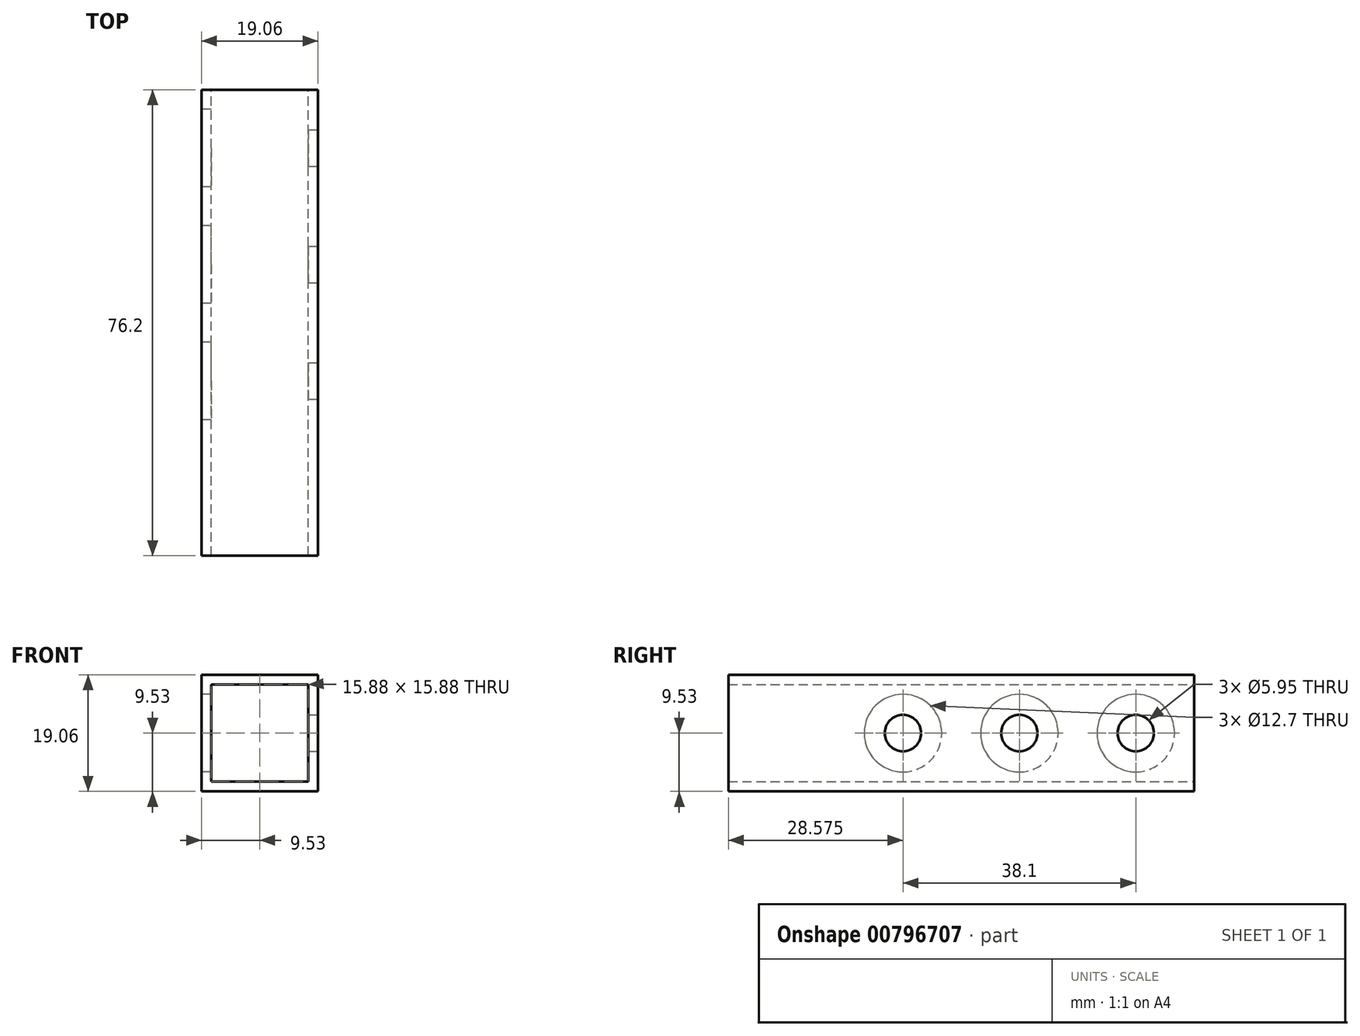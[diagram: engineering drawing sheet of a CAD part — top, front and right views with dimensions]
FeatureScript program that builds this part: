
annotation { "Feature Type Name" : "Feature", "Feature Type Description" : "" }
export const myFeature = defineFeature(function(context is Context, id is Id, definition is map)
    precondition{}
    {
        {
            var Q0;
            Q0=qCreatedBy(makeId("Front.planeOp"),FACE);
            var sketch = newSketch(context, id + "F0", { "sketchPlane" : qUnion([Q0])});
            skLineSegment(sketch, "E0.bottom", {"start": v(-9.52, 9.53) * mm, "end": v(9.53, 9.53) * mm});
            skLineSegment(sketch, "E0.top", {"start": v(-9.53, -9.53) * mm, "end": v(9.52, -9.53) * mm});
            skLineSegment(sketch, "E0.left", {"start": v(-9.52, 9.53) * mm, "end": v(-9.53, -9.52) * mm});
            skLineSegment(sketch, "E0.right", {"start": v(9.53, 9.53) * mm, "end": v(9.52, -9.52) * mm});
            skPoint(sketch, "E0.middle", {"position": v(0, 0) * mm});
            skLineSegment(sketch, "E1.bottom", {"start": v(-7.94, 7.94) * mm, "end": v(7.94, 7.94) * mm});
            skLineSegment(sketch, "E1.top", {"start": v(-7.94, -7.94) * mm, "end": v(7.94, -7.94) * mm});
            skLineSegment(sketch, "E1.left", {"start": v(-7.94, 7.94) * mm, "end": v(-7.94, -7.94) * mm});
            skLineSegment(sketch, "E1.right", {"start": v(7.94, 7.94) * mm, "end": v(7.94, -7.94) * mm});
            skSolve(sketch);
        }
        {
            var Q0;
            Q0=qSketchRegion(id+"F0",true);
            extrude(context, id + "F1", {"entities" : qUnion([Q0]), "depth" : 76.2 * mm, "offsetDistance" : 25.4 * mm});
        }
        {
            var Q0;
            Q0=makeQuery(id+"F1.opExtrude","SWEPT_FACE",FACE,{"disambiguationData":[OSD([sQuery(id+"F0.wireOp",EDGE,"E0.right")])]});
            var sketch = newSketch(context, id + "F2", { "sketchPlane" : qUnion([Q0])});
            skPoint(sketch, "E2", {"position": v(-9.53, 0) * mm});
            skPoint(sketch, "E3", {"position": v(-28.57, 0) * mm});
            skPoint(sketch, "E4", {"position": v(-47.62, 0) * mm});
            skSolve(sketch);
        }
        {
            var Q0;
            Q0=sQuery(id+"F2.wireOp",VERTEX,"E2");
            var Q1;
            Q1=sQuery(id+"F2.wireOp",VERTEX,"E3");
            var Q2;
            Q2=sQuery(id+"F2.wireOp",VERTEX,"E4");
            var Q3;
            Q3=makeQuery(id+"F1.opExtrude","SWEPT_BODY",BODY,{"disambiguationData":[OSD([sQuery(id+"F0.wireOp",EDGE,"E0.bottom"),sQuery(id+"F0.wireOp",EDGE,"E0.top"),sQuery(id+"F0.wireOp",EDGE,"E0.left"),sQuery(id+"F0.wireOp",EDGE,"E0.right"),sQuery(id+"F0.wireOp",EDGE,"E1.bottom"),sQuery(id+"F0.wireOp",EDGE,"E1.top"),sQuery(id+"F0.wireOp",EDGE,"E1.left"),sQuery(id+"F0.wireOp",EDGE,"E1.right")])]});
            hole(context, id + "F3", {"style" : HoleStyle.SIMPLE, "endStyle" : HoleEndStyle.BLIND, "holeDiameter" : 5.95 * mm, "majorDiameter" : 6.35 * mm, "holeDepth" : 6.35 * mm, "isTappedThrough" : true, "tappedDepth" : 12.7 * mm, "tapClearance" : 3, "startFromSketch" : true, "locations" : qUnion([Q0, Q1, Q2]), "scope" : qUnion([Q3])});
        }
        {
            var Q0;
            Q0=makeQuery(id+"F1.opExtrude","SWEPT_FACE",FACE,{"disambiguationData":[OSD([sQuery(id+"F0.wireOp",EDGE,"E0.left")])]});
            var sketch = newSketch(context, id + "F4", { "sketchPlane" : qUnion([Q0])});
            skPoint(sketch, "E5", {"position": v(9.53, 0) * mm});
            skPoint(sketch, "E6", {"position": v(28.57, 0) * mm});
            skPoint(sketch, "E7", {"position": v(47.62, 0) * mm});
            skSolve(sketch);
        }
        {
            var Q0;
            Q0=sQuery(id+"F4.wireOp",VERTEX,"E5");
            var Q1;
            Q1=sQuery(id+"F4.wireOp",VERTEX,"E6");
            var Q2;
            Q2=sQuery(id+"F4.wireOp",VERTEX,"E7");
            var Q3;
            Q3=makeQuery(id+"F1.opExtrude","SWEPT_BODY",BODY,{"disambiguationData":[OSD([sQuery(id+"F0.wireOp",EDGE,"E0.bottom"),sQuery(id+"F0.wireOp",EDGE,"E0.top"),sQuery(id+"F0.wireOp",EDGE,"E0.left"),sQuery(id+"F0.wireOp",EDGE,"E0.right"),sQuery(id+"F0.wireOp",EDGE,"E1.bottom"),sQuery(id+"F0.wireOp",EDGE,"E1.top"),sQuery(id+"F0.wireOp",EDGE,"E1.left"),sQuery(id+"F0.wireOp",EDGE,"E1.right")])]});
            hole(context, id + "F5", {"style" : HoleStyle.SIMPLE, "endStyle" : HoleEndStyle.BLIND, "holeDiameter" : 12.7 * mm, "majorDiameter" : 6.35 * mm, "holeDepth" : 6.35 * mm, "isTappedThrough" : true, "tappedDepth" : 12.7 * mm, "tapClearance" : 3, "startFromSketch" : true, "locations" : qUnion([Q0, Q1, Q2]), "scope" : qUnion([Q3])});
        }
    });
